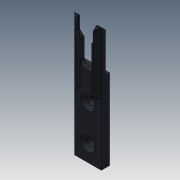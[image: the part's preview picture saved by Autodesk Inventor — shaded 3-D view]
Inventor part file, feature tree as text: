
AUTODESK INVENTOR PART (.ipt)
format: ipt  version: 2018.3 (Build 223284000, 284)  size: 219,648 bytes
history: native  units: in
note: dims shown in document units (in); Inventor stores cm internally (conversion verified against a paired STEP export)
features: sketch x6, extrude x6, hole x3, fillet x3, chamfer x3, projected_geometry x2
ambient origin geometry x8: Origin, YZ Plane, XZ Plane, XY Plane, X Axis, Y Axis, Z Axis, Center Point
bodies: Solid1 (feature_tree)
feature tree (23):
  sketch  "Sketch1"  dims[d0=1.5in d1=0.325in]
  extrude  "Extrusion1"  Depth=0.325in
  hole  "Hole2"  [1 undecoded]
  extrude  "Extrusion2"  Depth=0.302in
  extrude  "Extrusion3"  Depth=0.19in
  fillet  "Fillet1"  Radius=0.151in
  fillet  "Fillet2"  Radius=0.095in
  extrude  "Extrusion5"  Depth=0.1in TaperAngle=0.0deg
  chamfer  "Chamfer1"  Distance=0.19in
  chamfer  "Chamfer2"  Distance=0.35in
  sketch  "Sketch7"  dims[d21=0.225in d22=0.19in d23=0.35in d24=0.175in d25=0.05in d26=0.0in d27=0.0312in d28=0.0312in d29=0.05in d30=0.125in d31=45.0deg d32=0.04in d33=0.125in d34=45.0deg d35=0.0625in d40=0.05in d41=0.75in d42=0.173in d43=0.25in d44=90.0deg d45=1.0in d46=0.8108in d50=0.5in d51=0.225in d52=0.0in d53=0.05in d54=0.0in d55=0.0in d56=0.05in d57=0.0in d58=0.0in d59=1.0in d60=1.0in d61=0.094in d62=0.75in d63=0.173in d64=0.25in d65=90.0deg d66=1.0in d67=0.8108in d68=1.0in d69=1.0in d70=0.094in d71=0.75in d72=0.173in d73=0.25in d74=90.0deg d75=1.0in d76=0.8108in d77=0.05in d78=0.0in d79=0.05in d80=0.125in d81=45.0deg]
  extrude  "Extrusion6"  Depth=0.05in
  hole  "Hole3"  [1 undecoded]
  hole  "Hole4"  [1 undecoded]
  extrude  "Extrusion7"  Depth=0.0312in
  fillet  "Fillet3"  Radius=0.05in
  chamfer  "Chamfer4"  Distance=0.04in Angle=45.0deg
  sketch  "Sketch2"  dims[d2=0.1969in d3=0.4331in]
  sketch  "Sketch3"  dims[d4=0.15in d5=0.0in d13=0.302in]
  projected_geometry  "Projected Loop1"
  sketch  "Sketch5"  dims[d14=0.245in d15=0.19in d16=0.151in d17=0.095in]
  sketch  "Sketch6"  dims[d18=0.962in d19=0.1in d20=0.0in]
  projected_geometry  "Projected Loop3"
note: 3 required parameter values undecoded (feature->parameter linkage not recoverable at this tier; creation-order binding heuristic only, values carry confidence <= 0.55)
